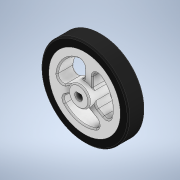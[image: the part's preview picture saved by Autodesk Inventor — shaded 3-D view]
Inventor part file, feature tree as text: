
AUTODESK INVENTOR PART (.ipt)
format: ipt  version: 2020 (Build 240168000, 168)  size: 373,248 bytes
history: native  units: mm
features: extrude x3, sketch x3, fillet x2, projected_geometry x2, chamfer x1
ambient origin geometry x8: Origin, YZ Plane, XZ Plane, XY Plane, X Axis, Y Axis, Z Axis, Center Point
bodies: Solid1 (feature_tree), Solid2 (feature_tree)
feature tree (11):
  extrude  "Extrusion1"  Depth=21.0mm
  fillet  "Fillet1"  Radius=8.0mm
  extrude  "Extrusion2"  Depth=3.0mm
  extrude  "Extrusion3"  Depth=0.5mm TaperAngle=360.0deg
  chamfer  "Chamfer1"  Distance=3.0mm
  fillet  "Fillet2"  Radius=1.17mm
  sketch  "Sketch1"  dims[d0=27.3mm d1=21.0mm d2=8.0mm]
  sketch  "Sketch2"  dims[d3=120.0deg d4=3.0mm]
  projected_geometry  "Projected Loop1"
  sketch  "Sketch3"  dims[d5=3.0mm d6=30.0mm d8=360.0deg d10=3.0mm d11=1.17mm d12=6.4mm d13=0.0mm d14=2.0mm d15=2.25mm d16=0.0mm d17=33.6mm d18=2.25mm d19=0.0mm d20=0.5mm d21=2.0mm d22=45.0deg d23=0.5mm]
  projected_geometry  "Projected Loop2"
